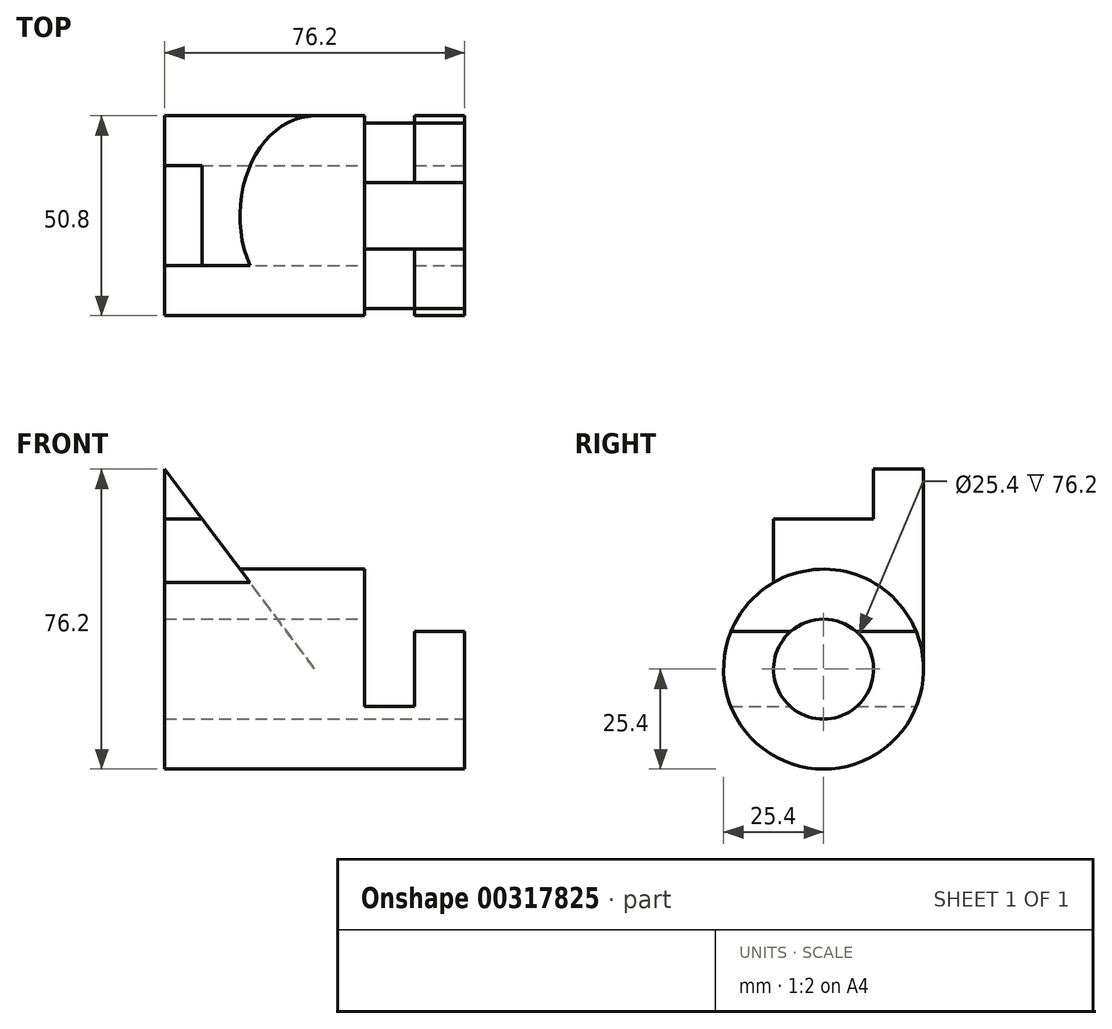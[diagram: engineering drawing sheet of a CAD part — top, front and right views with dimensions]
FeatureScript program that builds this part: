
annotation { "Feature Type Name" : "Feature", "Feature Type Description" : "" }
export const myFeature = defineFeature(function(context is Context, id is Id, definition is map)
    precondition{}
    {
        {
            var Q0;
            Q0=qCreatedBy(makeId("Front.planeOp"),FACE);
            var sketch = newSketch(context, id + "F0", { "sketchPlane" : qUnion([Q0])});
            skLineSegment(sketch, "E0", {"start": v(0, 0) * mm, "end": v(0, 50.8) * mm});
            skLineSegment(sketch, "E1", {"start": v(0, 50.8) * mm, "end": v(38.1, 0) * mm});
            skLineSegment(sketch, "E2", {"start": v(38.1, 0) * mm, "end": v(0, 0) * mm});
            skSolve(sketch);
        }
        {
            var Q0;
            Q0 = qSketchRegion(id + "F0", true);
            extrude(context, id + "F1", {"entities" : qUnion([Q0]), "depth" : 38.1 * mm});
        }
        {
            var Q0;
            Q0=qCreatedBy(makeId("Right.planeOp"),FACE);
            var sketch = newSketch(context, id + "F2", { "sketchPlane" : qUnion([Q0])});
            skCircle(sketch, "E3", {"center": v(-25.4, 0) * mm, "radius": 25.4 * mm});
            skSolve(sketch);
        }
        {
            var Q0;
            Q0=makeQuery(id+"F2.imprint","IMPRINT",FACE,{"disambiguationData":[TD([[makeQuery(id+"F2.imprint","IMPRINT",EDGE,{"derivedFrom":sQuery(id+"F2.wireOp",EDGE,"E3")}),1.0]])]});
            var Q1;
            Q1=sQuery(id+"F2.wireOp",EDGE,"E3");
            extrude(context, id + "F3", {"entities" : qUnion([Q0]), "operationType" : NewBodyOperationType.ADD, "surfaceEntities" : qUnion([Q1]), "depth" : 76.2 * mm});
        }
        {
            var Q0;
            Q0=makeQuery(id+"F3.opExtrude","CAP_FACE",FACE,{"disambiguationData":[OSD([sQuery(id+"F2.wireOp",EDGE,"E3")])],"isStart":false});
            var sketch = newSketch(context, id + "F4", { "sketchPlane" : qUnion([Q0])});
            skCircle(sketch, "E4", {"center": v(-25.4, 0) * mm, "radius": 12.7 * mm});
            skSolve(sketch);
        }
        {
            var Q0;
            Q0=makeQuery(id+"F4.imprint","IMPRINT",FACE,{"disambiguationData":[TD([[makeQuery(id+"F4.imprint","IMPRINT",EDGE,{"derivedFrom":sQuery(id+"F4.wireOp",EDGE,"E4")}),1.0]])]});
            extrude(context, id + "F5", {"entities" : qUnion([Q0]), "operationType" : NewBodyOperationType.REMOVE, "oppositeDirection" : true, "depth" : 76.2 * mm});
        }
        {
            var Q0;
            Q0=makeQuery(id+"F3.opExtrude","CAP_FACE",FACE,{"disambiguationData":[OSD([sQuery(id+"F2.wireOp",EDGE,"E3")])],"isStart":false});
            var sketch = newSketch(context, id + "F6", { "sketchPlane" : qUnion([Q0])});
            skLineSegment(sketch, "E5", {"start": v(-33.8, 9.52) * mm, "end": v(-48.95, 9.52) * mm});
            skLineSegment(sketch, "E6", {"start": v(-17, 9.52) * mm, "end": v(-1.85, 9.52) * mm});
            skSolve(sketch);
        }
        {
            var Q0;
            {var subQ0=sQuery(id+"F6.wireOp",EDGE,"E5");Q0=makeQuery(id+"F6.imprint","IMPRINT",FACE,{"disambiguationData":[TD([[makeQuery(id+"F6.imprint","IMPRINT",EDGE,{"derivedFrom":subQ0}),-1.0]])]});}
            extrude(context, id + "F7", {"entities" : qUnion([Q0]), "operationType" : NewBodyOperationType.REMOVE, "oppositeDirection" : true, "depth" : 25.4 * mm});
        }
        {
            var Q0;
            Q0=makeQuery(id+"F3.boolean.opBoolean","MERGE",FACE,{"derivedFrom":[makeQuery(id+"F1.opExtrude","SWEPT_FACE",FACE,{"disambiguationData":[OSD([sQuery(id+"F0.wireOp",EDGE,"E0")])]}),makeQuery(id+"F3.opExtrude","CAP_FACE",FACE,{"disambiguationData":[OSD([sQuery(id+"F2.wireOp",EDGE,"E3")])],"isStart":true})]});
            var sketch = newSketch(context, id + "F8", { "sketchPlane" : qUnion([Q0])});
            skLineSegment(sketch, "E7", {"start": v(38.1, 38.1) * mm, "end": v(12.7, 38.1) * mm});
            skLineSegment(sketch, "E8", {"start": v(12.7, 38.1) * mm, "end": v(12.7, 50.8) * mm});
            skSolve(sketch);
        }
        {
            var Q0;
            {var subQ0=sQuery(id+"F8.wireOp",EDGE,"E7");Q0=makeQuery(id+"F8.imprint","IMPRINT",FACE,{"disambiguationData":[TD([[makeQuery(id+"F8.imprint","IMPRINT",EDGE,{"derivedFrom":subQ0}),-1.0]])]});}
            extrude(context, id + "F9", {"entities" : qUnion([Q0]), "operationType" : NewBodyOperationType.REMOVE, "oppositeDirection" : true, "depth" : 25.4 * mm});
        }
        {
            var Q0;
            Q0=qCreatedBy(makeId("Front.planeOp"),FACE);
            var sketch = newSketch(context, id + "F10", { "sketchPlane" : qUnion([Q0])});
            skLineSegment(sketch, "E9", {"start": v(50.8, 9.52) * mm, "end": v(50.8, -9.53) * mm});
            skLineSegment(sketch, "E10", {"start": v(50.8, -9.53) * mm, "end": v(63.5, -9.53) * mm});
            skLineSegment(sketch, "E11", {"start": v(63.5, -9.53) * mm, "end": v(63.5, 9.52) * mm});
            skLineSegment(sketch, "E12", {"start": v(50.8, 9.52) * mm, "end": v(63.5, 9.52) * mm});
            skSolve(sketch);
        }
        {
            var Q0;
            Q0=makeQuery(id+"F10.imprint","IMPRINT",FACE,{"disambiguationData":[TD([[makeQuery(id+"F10.imprint","IMPRINT",EDGE,{"derivedFrom":sQuery(id+"F10.wireOp",EDGE,"E9")}),1.0]])]});
            extrude(context, id + "F11", {"entities" : qUnion([Q0]), "operationType" : NewBodyOperationType.REMOVE, "depth" : 76.2 * mm});
        }
    });
